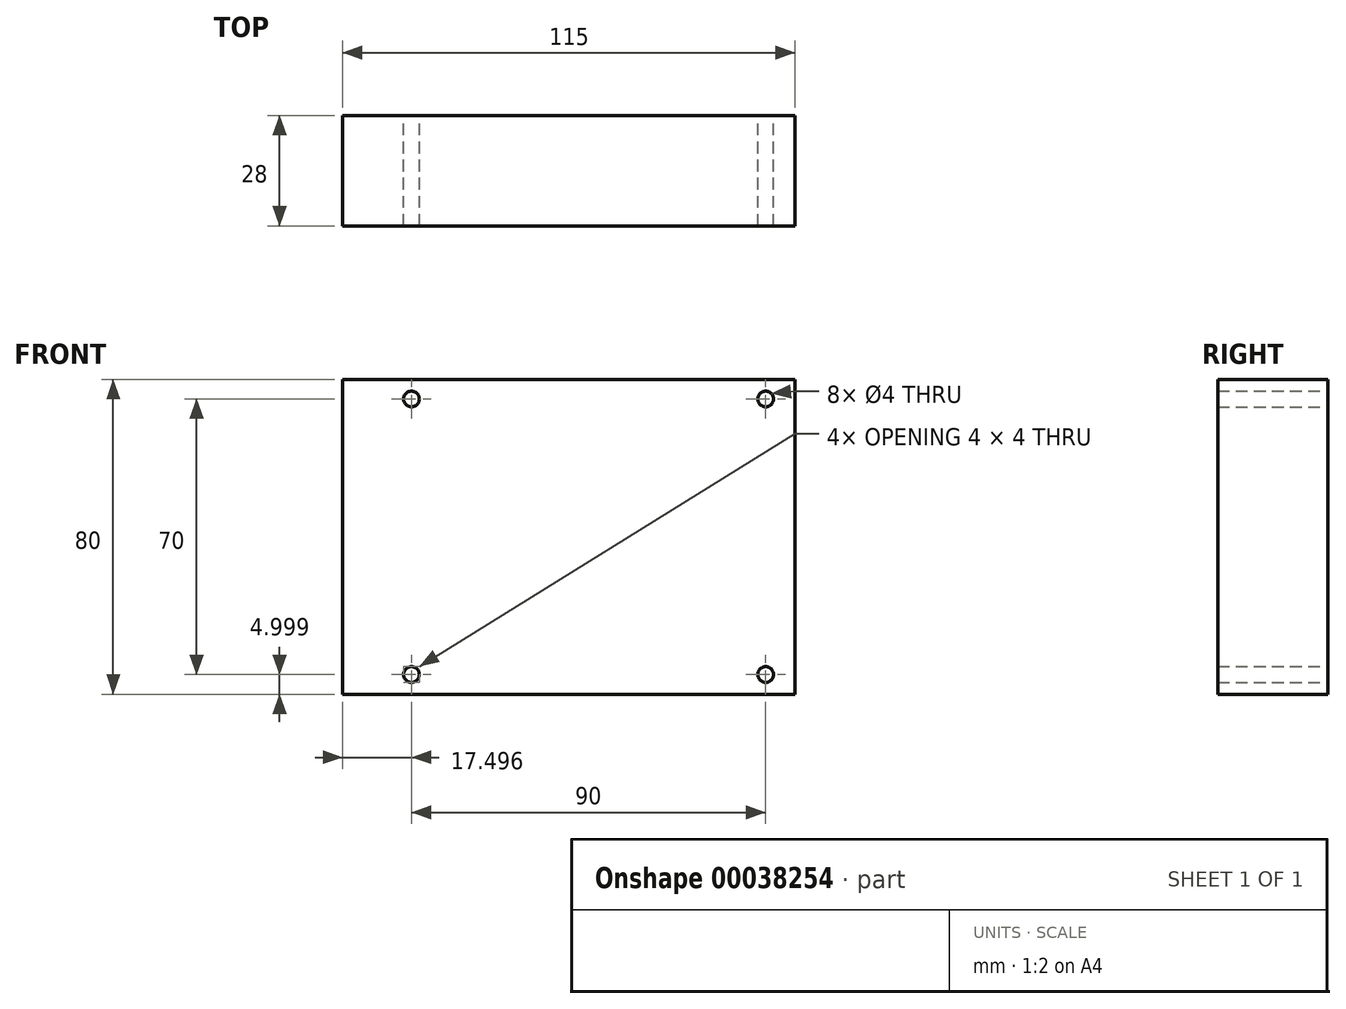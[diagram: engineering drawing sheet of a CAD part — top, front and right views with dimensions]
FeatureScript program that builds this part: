
annotation { "Feature Type Name" : "Feature", "Feature Type Description" : "" }
export const myFeature = defineFeature(function(context is Context, id is Id, definition is map)
    precondition{}
    {
        {
            var Q0;
            Q0=qCreatedBy(makeId("Front.planeOp"),FACE);
            var sketch = newSketch(context, id + "F0", { "sketchPlane" : qUnion([Q0])});
            skLineSegment(sketch, "E0.bottom", {"start": v(-77.47, -46.3) * mm, "end": v(37.53, -46.3) * mm});
            skLineSegment(sketch, "E0.top", {"start": v(-77.47, 33.7) * mm, "end": v(37.53, 33.7) * mm});
            skLineSegment(sketch, "E0.left", {"start": v(-77.47, -46.3) * mm, "end": v(-77.47, 33.7) * mm});
            skLineSegment(sketch, "E0.right", {"start": v(37.53, -46.3) * mm, "end": v(37.53, 33.7) * mm});
            skLineSegment(sketch, "E1", {"start": v(-59.97, 43.37) * mm, "end": v(-59.97, -60.1) * mm});
            skLineSegment(sketch, "E2", {"start": v(30.03, 42.16) * mm, "end": v(30.03, -58.64) * mm});
            skLineSegment(sketch, "E3", {"start": v(-68.92, 28.7) * mm, "end": v(58.11, 28.7) * mm});
            skLineSegment(sketch, "E4", {"start": v(-69.4, -41.3) * mm, "end": v(46.94, -41.3) * mm});
            skPoint(sketch, "E5", {"position": v(-59.97, 28.7) * mm});
            skPoint(sketch, "E6", {"position": v(30.03, 28.7) * mm});
            skPoint(sketch, "E7", {"position": v(30.03, -41.3) * mm});
            skPoint(sketch, "E8", {"position": v(-59.97, -41.3) * mm});
            skSolve(sketch);
        }
        {
            var Q0;
            {var subQ5=sQuery(id+"F0.wireOp",EDGE,"E0.left");Q0=makeQuery(id+"F0.imprint","IMPRINT",FACE,{"disambiguationData":[TD([[makeQuery(id+"F0.imprint","IMPRINT",EDGE,{"derivedFrom":subQ5}),-1.0]])]});}
            var Q1;
            {var subQ3=sQuery(id+"F0.wireOp",EDGE,"E1");var subQ5=sQuery(id+"F0.wireOp",EDGE,"E0.top");var subQ7=makeQuery(id+"F0.imprint","INTERSECT",VERTEX,{"derivedFrom":[subQ5,subQ3]});Q1=makeQuery(id+"F0.imprint","IMPRINT",FACE,{"disambiguationData":[TD([[makeQuery(id+"F0.imprint","IMPRINT",EDGE,{"disambiguationData":[TD([[subQ7,-1.0]])],"derivedFrom":subQ5}),-1.0]])]});}
            var Q2;
            {var subQ3=sQuery(id+"F0.wireOp",EDGE,"E1");var subQ5=sQuery(id+"F0.wireOp",EDGE,"E3");var subQ7=makeQuery(id+"F0.imprint","INTERSECT",VERTEX,{"derivedFrom":[subQ3,subQ5]});Q2=makeQuery(id+"F0.imprint","IMPRINT",FACE,{"disambiguationData":[TD([[makeQuery(id+"F0.imprint","IMPRINT",EDGE,{"disambiguationData":[TD([[subQ7,-1.0]])],"derivedFrom":subQ3}),1.0]])]});}
            var Q3;
            {var subQ0=sQuery(id+"F0.wireOp",EDGE,"E4");var subQ3=sQuery(id+"F0.wireOp",EDGE,"E0.right");var subQ4=makeQuery(id+"F0.imprint","INTERSECT",VERTEX,{"derivedFrom":[subQ3,subQ0]});Q3=makeQuery(id+"F0.imprint","IMPRINT",FACE,{"disambiguationData":[TD([[makeQuery(id+"F0.imprint","IMPRINT",EDGE,{"disambiguationData":[TD([[subQ4,-1.0]])],"derivedFrom":subQ3}),1.0]])]});}
            var Q4;
            {var subQ3=sQuery(id+"F0.wireOp",EDGE,"E0.right");var subQ5=sQuery(id+"F0.wireOp",EDGE,"E0.top");var subQ7=makeQuery(id+"F0.imprint","INTERSECT",VERTEX,{"derivedFrom":[subQ5,subQ3]});Q4=makeQuery(id+"F0.imprint","IMPRINT",FACE,{"disambiguationData":[TD([[makeQuery(id+"F0.imprint","IMPRINT",EDGE,{"disambiguationData":[TD([[subQ7,1.0]])],"derivedFrom":subQ5}),-1.0]])]});}
            var Q5;
            {var subQ3=sQuery(id+"F0.wireOp",EDGE,"E0.bottom");var subQ5=sQuery(id+"F0.wireOp",EDGE,"E1");var subQ7=makeQuery(id+"F0.imprint","INTERSECT",VERTEX,{"derivedFrom":[subQ3,subQ5]});Q5=makeQuery(id+"F0.imprint","IMPRINT",FACE,{"disambiguationData":[TD([[makeQuery(id+"F0.imprint","IMPRINT",EDGE,{"disambiguationData":[TD([[subQ7,-1.0]])],"derivedFrom":subQ3}),1.0]])]});}
            var Q6;
            {var subQ3=sQuery(id+"F0.wireOp",EDGE,"E0.bottom");var subQ5=sQuery(id+"F0.wireOp",EDGE,"E0.right");var subQ7=makeQuery(id+"F0.imprint","INTERSECT",VERTEX,{"derivedFrom":[subQ3,subQ5]});Q6=makeQuery(id+"F0.imprint","IMPRINT",FACE,{"disambiguationData":[TD([[makeQuery(id+"F0.imprint","IMPRINT",EDGE,{"disambiguationData":[TD([[subQ7,1.0]])],"derivedFrom":subQ3}),1.0]])]});}
            extrude(context, id + "F1", {"entities" : qUnion([Q0, Q1, Q2, Q3, Q4, Q5, Q6]), "depth" : 28 * mm});
        }
        {
            var Q0;
            Q0=sQuery(id+"F0.wireOp",VERTEX,"E5");
            var Q1;
            Q1=sQuery(id+"F0.wireOp",VERTEX,"E6");
            var Q2;
            Q2=sQuery(id+"F0.wireOp",VERTEX,"E8");
            var Q3;
            Q3=sQuery(id+"F0.wireOp",VERTEX,"E7");
            var Q4;
            Q4=makeQuery(id+"F1.opExtrude","SWEPT_BODY",BODY,{"disambiguationData":[OSD([sQuery(id+"F0.wireOp",EDGE,"E0.bottom"),sQuery(id+"F0.wireOp",EDGE,"E0.top"),sQuery(id+"F0.wireOp",EDGE,"E0.left"),sQuery(id+"F0.wireOp",EDGE,"E0.right")])]});
            hole(context, id + "F2", {"style" : HoleStyle.SIMPLE, "holeDiameter" : 4 * mm, "endStyle" : HoleEndStyle.THROUGH, "oppositeDirection" : true, "locations" : qUnion([Q0, Q1, Q2, Q3]), "scope" : qUnion([Q4])});
        }
    });
